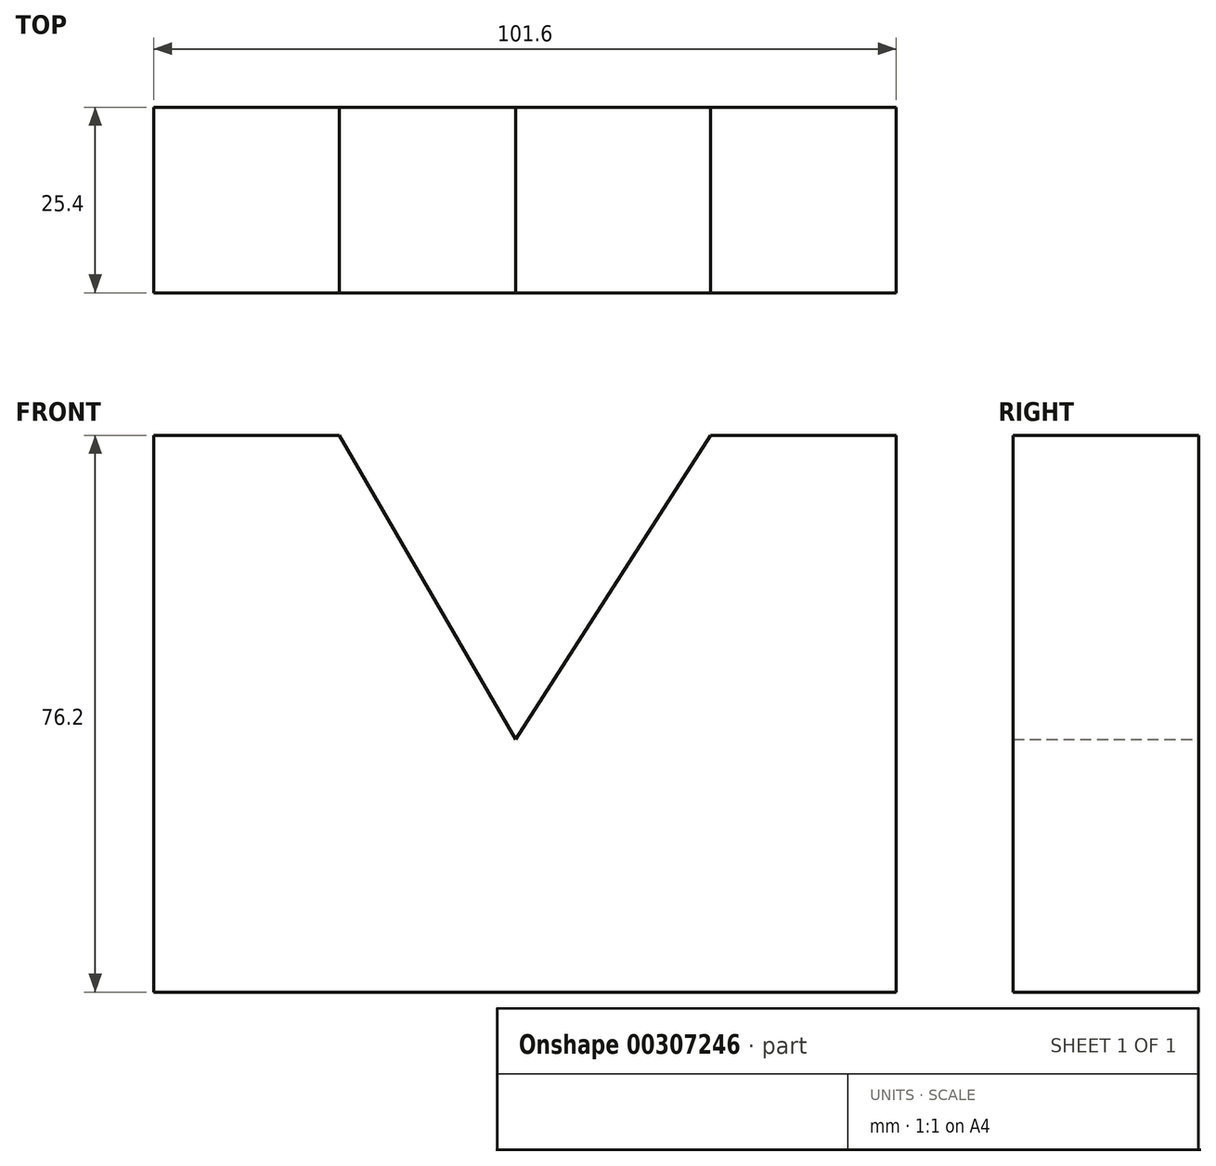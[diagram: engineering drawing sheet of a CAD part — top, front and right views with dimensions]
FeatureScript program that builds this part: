
annotation { "Feature Type Name" : "Feature", "Feature Type Description" : "" }
export const myFeature = defineFeature(function(context is Context, id is Id, definition is map)
    precondition{}
    {
        {
            var Q0;
            Q0=qCreatedBy(makeId("Front.planeOp"),FACE);
            var sketch = newSketch(context, id + "F0", { "sketchPlane" : qUnion([Q0])});
            skLineSegment(sketch, "E0", {"start": v(-48.07, 32.4) * mm, "end": v(-48.07, -43.8) * mm});
            skLineSegment(sketch, "E1", {"start": v(-48.07, -43.8) * mm, "end": v(53.53, -43.8) * mm});
            skLineSegment(sketch, "E2", {"start": v(53.53, -43.8) * mm, "end": v(53.53, 32.4) * mm});
            skLineSegment(sketch, "E3", {"start": v(53.53, 32.4) * mm, "end": v(28.13, 32.4) * mm});
            skLineSegment(sketch, "E4", {"start": v(-48.07, 32.4) * mm, "end": v(-22.67, 32.4) * mm});
            skLineSegment(sketch, "E5", {"start": v(-22.67, 32.4) * mm, "end": v(1.43, -9.2) * mm});
            skLineSegment(sketch, "E6", {"start": v(1.43, -9.2) * mm, "end": v(28.13, 32.4) * mm});
            skSolve(sketch);
        }
        {
            var Q0;
            Q0=makeQuery(id+"F0.imprint","IMPRINT",FACE,{"disambiguationData":[TD([[makeQuery(id+"F0.imprint","IMPRINT",EDGE,{"derivedFrom":sQuery(id+"F0.wireOp",EDGE,"E0")}),1.0]])]});
            extrude(context, id + "F1", {"entities" : qUnion([Q0]), "depth" : 25.4 * mm});
        }
    });
